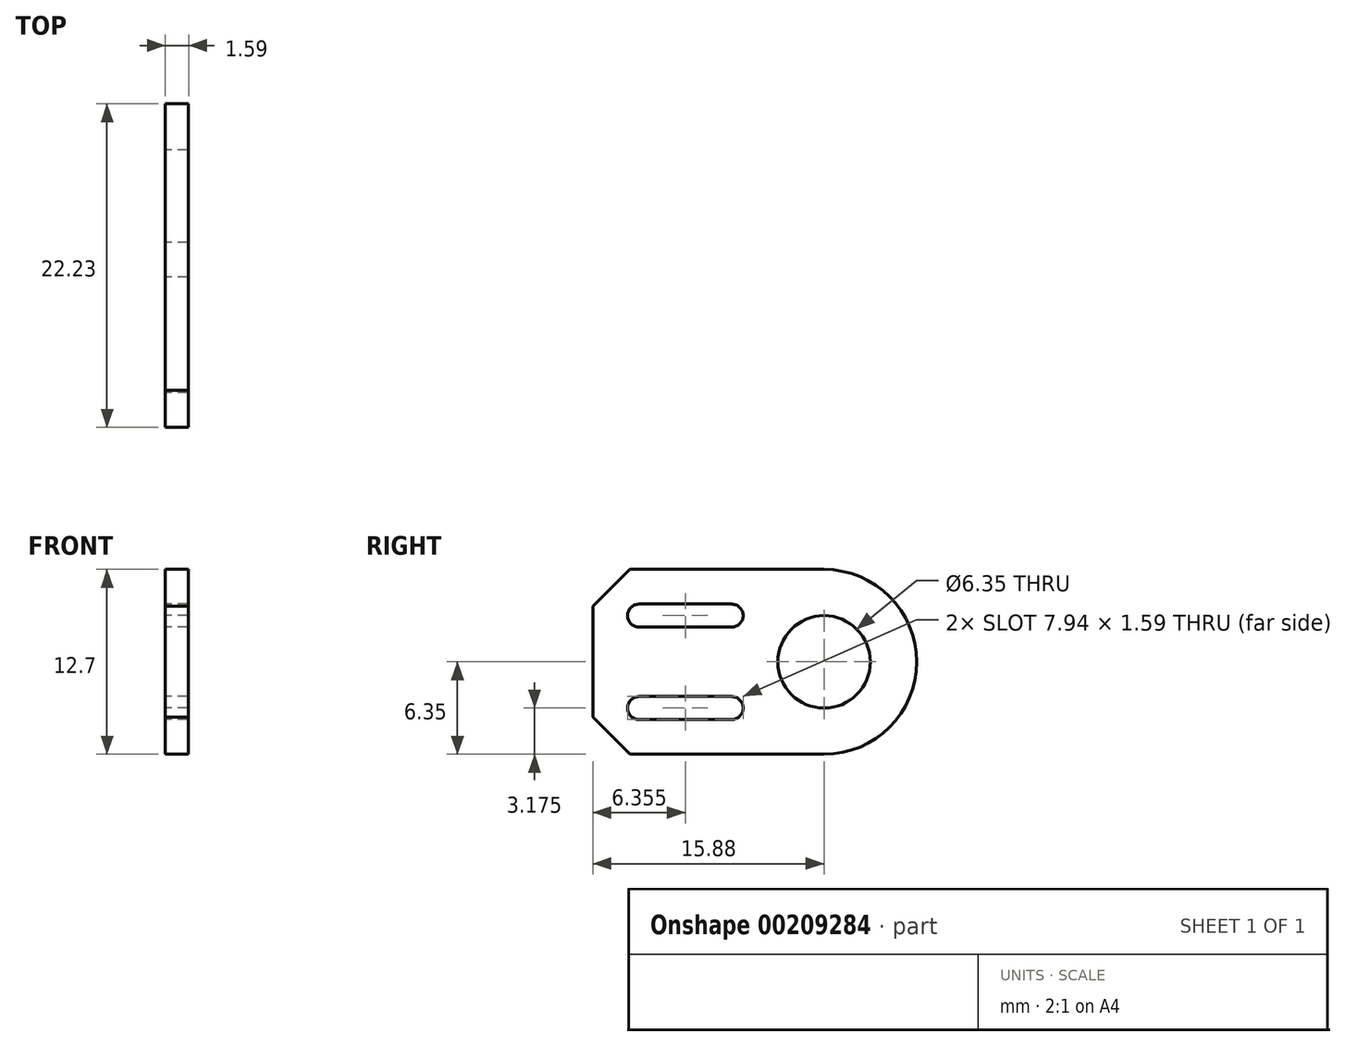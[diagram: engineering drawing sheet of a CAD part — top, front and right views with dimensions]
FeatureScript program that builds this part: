
annotation { "Feature Type Name" : "Feature", "Feature Type Description" : "" }
export const myFeature = defineFeature(function(context is Context, id is Id, definition is map)
    precondition{}
    {
        {
            var Q0;
            Q0=qCreatedBy(makeId("Right.planeOp"),FACE);
            var sketch = newSketch(context, id + "F0", { "sketchPlane" : qUnion([Q0])});
            skCircle(sketch, "E0", {"center": v(0, 0) * mm, "radius": 6.35 * mm});
            skCircle(sketch, "E1", {"center": v(0, 0) * mm, "radius": 3.18 * mm});
            skLineSegment(sketch, "E2.bottom", {"start": v(0, 6.35) * mm, "end": v(-15.88, 6.35) * mm});
            skLineSegment(sketch, "E2.top", {"start": v(0, -6.35) * mm, "end": v(-15.87, -6.35) * mm});
            skLineSegment(sketch, "E2.left", {"start": v(0, 6.35) * mm, "end": v(0, -6.35) * mm});
            skLineSegment(sketch, "E2.right", {"start": v(-15.88, 6.35) * mm, "end": v(-15.87, -6.35) * mm});
            skLineSegment(sketch, "E3", {"start": v(-8.72, 3.18) * mm, "end": v(-27.86, 3.18) * mm, "construction": true});
            skLineSegment(sketch, "E4", {"start": v(-27.86, 3.18) * mm, "end": v(-27.86, -3.17) * mm, "construction": true});
            skLineSegment(sketch, "E5", {"start": v(-27.86, -3.17) * mm, "end": v(-8.94, -3.17) * mm, "construction": true});
            skLineSegment(sketch, "E6", {"start": v(-12.7, 4.83) * mm, "end": v(-12.7, -4.94) * mm, "construction": true});
            skLineSegment(sketch, "E7", {"start": v(-12.7, -4.94) * mm, "end": v(-6.35, -4.94) * mm, "construction": true});
            skLineSegment(sketch, "E8", {"start": v(-6.35, -4.94) * mm, "end": v(-6.35, 4.7) * mm, "construction": true});
            skCircle(sketch, "E9", {"center": v(-12.7, 3.18) * mm, "radius": 0.8 * mm});
            skCircle(sketch, "E10", {"center": v(-6.35, 3.18) * mm, "radius": 0.8 * mm});
            skCircle(sketch, "E11", {"center": v(-6.35, -3.17) * mm, "radius": 0.8 * mm});
            skCircle(sketch, "E12", {"center": v(-12.7, -3.17) * mm, "radius": 0.8 * mm});
            skLineSegment(sketch, "E13.bottom", {"start": v(-12.7, 3.97) * mm, "end": v(-6.35, 3.97) * mm});
            skLineSegment(sketch, "E13.top", {"start": v(-12.7, 2.38) * mm, "end": v(-6.35, 2.38) * mm});
            skLineSegment(sketch, "E13.left", {"start": v(-12.7, 3.97) * mm, "end": v(-12.7, 2.38) * mm});
            skLineSegment(sketch, "E13.right", {"start": v(-6.35, 3.97) * mm, "end": v(-6.35, 2.38) * mm});
            skLineSegment(sketch, "E14.bottom", {"start": v(-6.35, -2.38) * mm, "end": v(-12.7, -2.38) * mm});
            skLineSegment(sketch, "E14.top", {"start": v(-6.35, -3.97) * mm, "end": v(-12.7, -3.97) * mm});
            skLineSegment(sketch, "E14.left", {"start": v(-6.35, -2.38) * mm, "end": v(-6.35, -3.97) * mm});
            skLineSegment(sketch, "E14.right", {"start": v(-12.7, -2.38) * mm, "end": v(-12.7, -3.97) * mm});
            skLineSegment(sketch, "E15", {"start": v(-13.33, -6.35) * mm, "end": v(-15.87, -3.8) * mm});
            skLineSegment(sketch, "E16", {"start": v(-13.33, 6.35) * mm, "end": v(-15.88, 3.8) * mm});
            skSolve(sketch);
        }
        {
            var Q0;
            {var subQ0=sQuery(id+"F0.wireOp",EDGE,"E2.left");var subQ4=sQuery(id+"F0.wireOp",EDGE,"E1");var subQ5=makeQuery(id+"F0.imprint","INTERSECT",VERTEX,{"disambiguationData":[OD(0.0)],"derivedFrom":[subQ4,subQ0]});Q0=makeQuery(id+"F0.imprint","IMPRINT",FACE,{"disambiguationData":[TD([[makeQuery(id+"F0.imprint","IMPRINT",EDGE,{"disambiguationData":[TD([[subQ5,1.0]])],"derivedFrom":subQ4}),-1.0]])]});}
            var Q1;
            {var subQ0=sQuery(id+"F0.wireOp",EDGE,"E2.left");var subQ4=sQuery(id+"F0.wireOp",EDGE,"E1");var subQ5=makeQuery(id+"F0.imprint","INTERSECT",VERTEX,{"disambiguationData":[OD(0.0)],"derivedFrom":[subQ4,subQ0]});Q1=makeQuery(id+"F0.imprint","IMPRINT",FACE,{"disambiguationData":[TD([[makeQuery(id+"F0.imprint","IMPRINT",EDGE,{"disambiguationData":[TD([[subQ5,-1.0]])],"derivedFrom":subQ4}),-1.0]])]});}
            var Q2;
            {var subQ1=sQuery(id+"F0.wireOp",EDGE,"E13.bottom");Q2=makeQuery(id+"F0.imprint","IMPRINT",FACE,{"disambiguationData":[TD([[makeQuery(id+"F0.imprint","IMPRINT",EDGE,{"derivedFrom":subQ1}),1.0]])]});}
            extrude(context, id + "F1", {"entities" : qUnion([Q0, Q1, Q2]), "depth" : 1.59 * mm});
        }
    });
